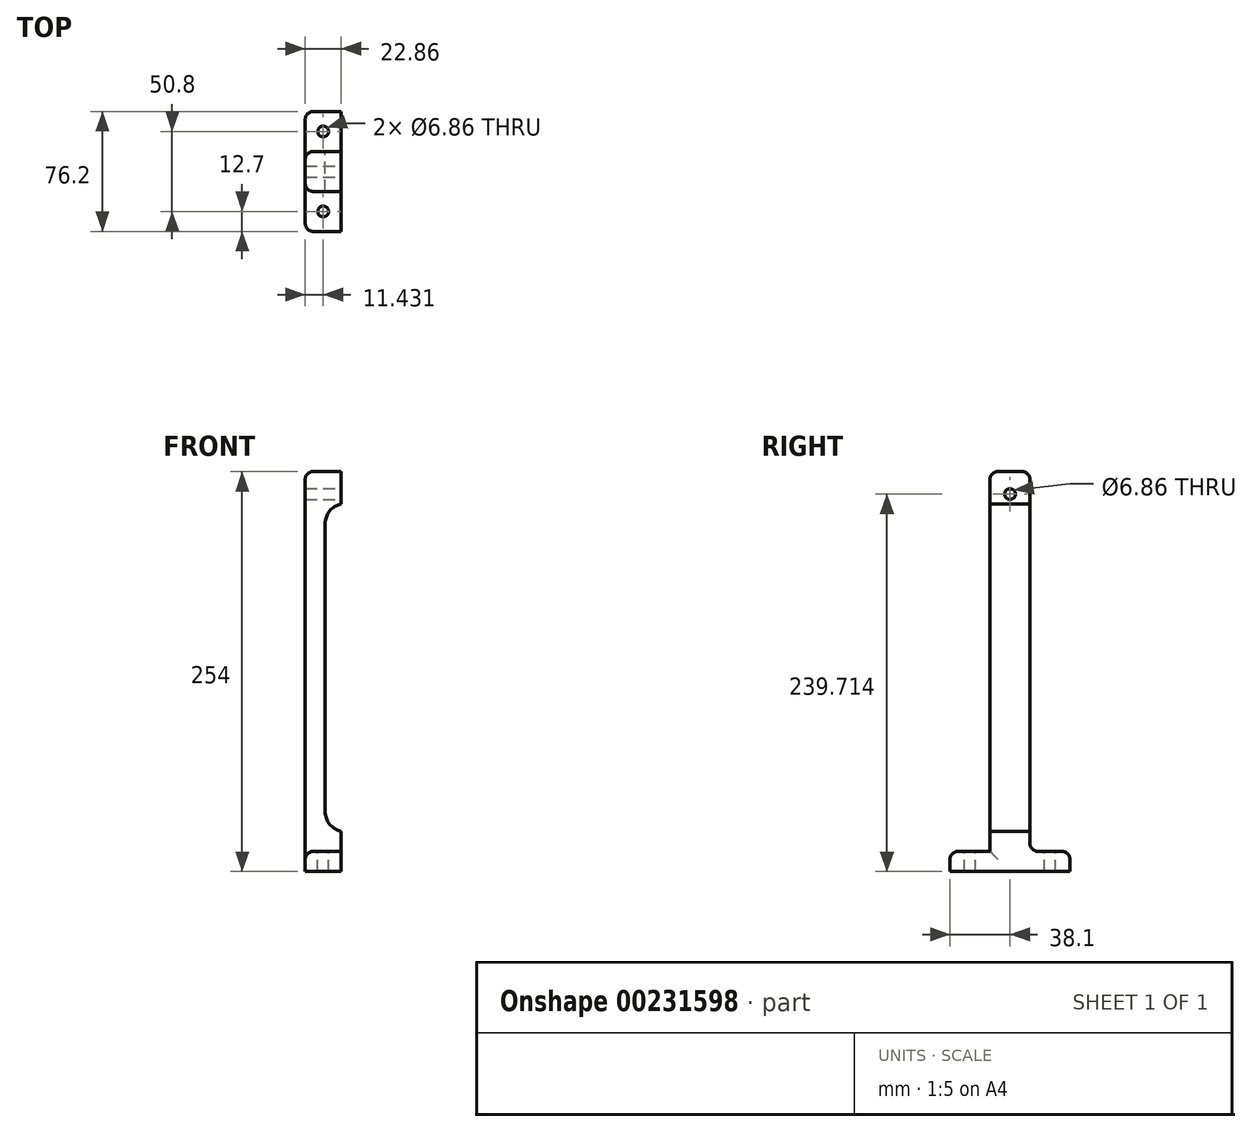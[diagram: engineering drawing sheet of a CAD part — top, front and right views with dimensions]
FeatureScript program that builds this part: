
annotation { "Feature Type Name" : "Feature", "Feature Type Description" : "" }
export const myFeature = defineFeature(function(context is Context, id is Id, definition is map)
    precondition{}
    {
        {
            var Q0;
            Q0=qCreatedBy(makeId("Front.planeOp"),FACE);
            var sketch = newSketch(context, id + "F0", { "sketchPlane" : qUnion([Q0])});
            skLineSegment(sketch, "E0.0", {"start": v(-25.4, 91.14) * mm, "end": v(-25.4, -91.42) * mm});
            skLineSegment(sketch, "E1", {"start": v(-25.4, 91.14) * mm, "end": v(-25.4, 124.52) * mm});
            skLineSegment(sketch, "E2.MirrorCS", {"start": v(-25.4, -91.14) * mm, "end": v(-25.4, -129.48) * mm});
            skArc(sketch, "E3", {"start": v(-2.54, 103.88) * mm, "mid": v(-9.84, 99.47) * mm, "end": v(-12.7, 91.44) * mm});
            skArc(sketch, "E4.MirrorCS", {"start": v(-2.54, -103.88) * mm, "mid": v(-9.84, -99.47) * mm, "end": v(-12.7, -91.44) * mm});
            skLineSegment(sketch, "E5", {"start": v(-12.7, 91.44) * mm, "end": v(-12.7, -91.44) * mm});
            skLineSegment(sketch, "E6.MirrorCS", {"start": v(-2.54, 124.52) * mm, "end": v(-2.54, 103.88) * mm});
            skLineSegment(sketch, "E7", {"start": v(-2.54, -129.48) * mm, "end": v(-25.4, -129.48) * mm});
            skLineSegment(sketch, "E8", {"start": v(-2.54, -103.88) * mm, "end": v(-2.54, -129.48) * mm});
            skLineSegment(sketch, "E9", {"start": v(-25.4, 124.52) * mm, "end": v(-2.54, 124.52) * mm});
            skSolve(sketch);
        }
        {
            var Q0;
            Q0=qSketchRegion(id+"F0",true);
            extrude(context, id + "F1", {"entities" : qUnion([Q0]), "depth" : 25.4 * mm});
        }
        {
            var Q0;
            Q0=makeQuery(id+"F1.opExtrude","SWEPT_FACE",FACE,{"disambiguationData":[OSD([sQuery(id+"F0.wireOp",EDGE,"E6.MirrorCS")])]});
            var sketch = newSketch(context, id + "F2", { "sketchPlane" : qUnion([Q0])});
            skCircle(sketch, "E10", {"center": v(-12.7, 110.23) * mm, "radius": 3.43 * mm});
            skCircle(sketch, "E11.MirrorC", {"center": v(-12.7, -110.23) * mm, "radius": 3.43 * mm});
            skSolve(sketch);
        }
        {
            var Q0;
            Q0=makeQuery(id+"F2.imprint","IMPRINT",FACE,{"disambiguationData":[TD([[makeQuery(id+"F2.imprint","IMPRINT",EDGE,{"derivedFrom":sQuery(id+"F2.wireOp",EDGE,"E11.MirrorC")}),-1.0]])]});
            var Q1;
            Q1=makeQuery(id+"F2.imprint","IMPRINT",FACE,{"disambiguationData":[TD([[makeQuery(id+"F2.imprint","IMPRINT",EDGE,{"derivedFrom":sQuery(id+"F2.wireOp",EDGE,"E10")}),1.0]])]});
            extrude(context, id + "F3", {"entities" : qUnion([Q0, Q1]), "operationType" : NewBodyOperationType.REMOVE, "oppositeDirection" : true, "depth" : 147.32 * mm});
        }
        {
            var Q0;
            Q0=makeQuery(id+"F1.opExtrude","CAP_FACE",FACE,{"disambiguationData":[OSD([sQuery(id+"F0.wireOp",EDGE,"E0.0"),sQuery(id+"F0.wireOp",EDGE,"E1"),sQuery(id+"F0.wireOp",EDGE,"E2.MirrorCS"),sQuery(id+"F0.wireOp",EDGE,"E3"),sQuery(id+"F0.wireOp",EDGE,"E4.MirrorCS"),sQuery(id+"F0.wireOp",EDGE,"E5"),sQuery(id+"F0.wireOp",EDGE,"E6.MirrorCS"),sQuery(id+"F0.wireOp",EDGE,"E7"),sQuery(id+"F0.wireOp",EDGE,"E8"),sQuery(id+"F0.wireOp",EDGE,"E9")])],"isStart":false});
            var sketch = newSketch(context, id + "F4", { "sketchPlane" : qUnion([Q0])});
            skLineSegment(sketch, "E12.bottom", {"start": v(-2.54, -129.48) * mm, "end": v(-25.4, -129.48) * mm});
            skLineSegment(sketch, "E12.top", {"start": v(-2.54, -116.78) * mm, "end": v(-25.4, -116.78) * mm});
            skLineSegment(sketch, "E12.left", {"start": v(-2.54, -129.48) * mm, "end": v(-2.54, -116.78) * mm});
            skLineSegment(sketch, "E12.right", {"start": v(-25.4, -129.48) * mm, "end": v(-25.4, -116.78) * mm});
            skSolve(sketch);
        }
        {
            var Q0;
            Q0=makeQuery(id+"F4.imprint","IMPRINT",FACE,{"disambiguationData":[TD([[makeQuery(id+"F4.imprint","IMPRINT",EDGE,{"derivedFrom":sQuery(id+"F4.wireOp",EDGE,"E12.bottom")}),-1.0]])]});
            extrude(context, id + "F5", {"entities" : qUnion([Q0]), "operationType" : NewBodyOperationType.ADD, "depth" : 25.4 * mm});
        }
        {
            var Q0;
            Q0=makeQuery(id+"F5.opExtrude","CAP_FACE",FACE,{"disambiguationData":[OSD([sQuery(id+"F4.wireOp",EDGE,"E12.bottom"),sQuery(id+"F4.wireOp",EDGE,"E12.top"),sQuery(id+"F4.wireOp",EDGE,"E12.left"),sQuery(id+"F4.wireOp",EDGE,"E12.right")])],"isStart":false});
            extrude(context, id + "F6", {"entities" : qUnion([Q0]), "operationType" : NewBodyOperationType.ADD, "oppositeDirection" : true, "depth" : 76.2 * mm});
        }
        {
            var Q0;
            Q0=makeQuery(id+"F6.opExtrude","SWEPT_FACE",FACE,{"disambiguationData":[OSD([sQuery(id+"F4.wireOp",EDGE,"E12.top")])]});
            var sketch = newSketch(context, id + "F7", { "sketchPlane" : qUnion([Q0])});
            skCircle(sketch, "E13", {"center": v(-13.97, 12.7) * mm, "radius": 3.43 * mm});
            skPoint(sketch, "E13.centerSnap0", {"position": v(-25.4, 12.7) * mm});
            skPoint(sketch, "E13.centerSnap1", {"position": v(-13.97, 25.4) * mm});
            skLineSegment(sketch, "E14", {"start": v(-13.97, 25.4) * mm, "end": v(-13.97, -38.1) * mm});
            skCircle(sketch, "E15", {"center": v(-13.97, -38.1) * mm, "radius": 3.43 * mm});
            skSolve(sketch);
        }
        {
            var Q0;
            {var subQ0=sQuery(id+"F7.wireOp",EDGE,"E14");var subQ1=sQuery(id+"F7.wireOp",EDGE,"E13");var subQ2=makeQuery(id+"F7.imprint","INTERSECT",VERTEX,{"disambiguationData":[OD(0.0)],"derivedFrom":[subQ1,subQ0]});Q0=makeQuery(id+"F7.imprint","IMPRINT",FACE,{"disambiguationData":[TD([[makeQuery(id+"F7.imprint","IMPRINT",EDGE,{"disambiguationData":[TD([[subQ2,-1.0]])],"derivedFrom":subQ1}),1.0]])]});}
            var Q1;
            Q1=makeQuery(id+"F7.imprint","IMPRINT",FACE,{"disambiguationData":[TD([[makeQuery(id+"F7.imprint","IMPRINT",EDGE,{"derivedFrom":sQuery(id+"F7.wireOp",EDGE,"E15")}),1.0]])]});
            var Q2;
            {var subQ0=sQuery(id+"F7.wireOp",EDGE,"E14");var subQ1=sQuery(id+"F7.wireOp",EDGE,"E13");var subQ2=makeQuery(id+"F7.imprint","INTERSECT",VERTEX,{"disambiguationData":[OD(0.0)],"derivedFrom":[subQ1,subQ0]});Q2=makeQuery(id+"F7.imprint","IMPRINT",FACE,{"disambiguationData":[TD([[makeQuery(id+"F7.imprint","IMPRINT",EDGE,{"disambiguationData":[TD([[subQ2,1.0]])],"derivedFrom":subQ1}),1.0]])]});}
            extrude(context, id + "F8", {"entities" : qUnion([Q0, Q1, Q2]), "operationType" : NewBodyOperationType.REMOVE, "oppositeDirection" : true, "depth" : 25.4 * mm});
        }
        {
            var Q0;
            Q0=makeQuery(id+"F1.opExtrude","CAP_EDGE",EDGE,{"disambiguationData":[OSD([sQuery(id+"F0.wireOp",EDGE,"E9")])],"isStart":false});
            var Q1;
            Q1=makeQuery(id+"F1.opExtrude","SWEPT_EDGE",EDGE,{"disambiguationData":[OSD([sQuery(id+"F0.wireOp",EDGE,"E1"),sQuery(id+"F0.wireOp",EDGE,"E9")])]});
            var Q2;
            Q2=makeQuery(id+"F1.opExtrude","CAP_EDGE",EDGE,{"disambiguationData":[OSD([sQuery(id+"F0.wireOp",EDGE,"E9")])],"isStart":true});
            var Q3;
            Q3=makeQuery(id+"F1.opExtrude","CAP_EDGE",EDGE,{"disambiguationData":[OSD([sQuery(id+"F0.wireOp",EDGE,"E0.0"),sQuery(id+"F0.wireOp",EDGE,"E1"),sQuery(id+"F0.wireOp",EDGE,"E2.MirrorCS")])],"isStart":false});
            var Q4;
            Q4=makeQuery(id+"F1.opExtrude","CAP_EDGE",EDGE,{"disambiguationData":[OSD([sQuery(id+"F0.wireOp",EDGE,"E0.0"),sQuery(id+"F0.wireOp",EDGE,"E1"),sQuery(id+"F0.wireOp",EDGE,"E2.MirrorCS")])],"isStart":true});
            var Q5;
            Q5=makeQuery(id+"F6.boolean.opBoolean","INTERSECT",EDGE,{"derivedFrom":[makeQuery(id+"F1.opExtrude","CAP_FACE",FACE,{"disambiguationData":[OSD([sQuery(id+"F0.wireOp",EDGE,"E0.0"),sQuery(id+"F0.wireOp",EDGE,"E1"),sQuery(id+"F0.wireOp",EDGE,"E2.MirrorCS"),sQuery(id+"F0.wireOp",EDGE,"E3"),sQuery(id+"F0.wireOp",EDGE,"E4.MirrorCS"),sQuery(id+"F0.wireOp",EDGE,"E5"),sQuery(id+"F0.wireOp",EDGE,"E6.MirrorCS"),sQuery(id+"F0.wireOp",EDGE,"E7"),sQuery(id+"F0.wireOp",EDGE,"E8"),sQuery(id+"F0.wireOp",EDGE,"E9")])],"isStart":true}),makeQuery(id+"F6.opExtrude","SWEPT_FACE",FACE,{"disambiguationData":[OSD([sQuery(id+"F4.wireOp",EDGE,"E12.top")])]})]});
            var Q6;
            Q6=makeQuery(id+"F6.opExtrude","CAP_EDGE",EDGE,{"disambiguationData":[OSD([sQuery(id+"F4.wireOp",EDGE,"E12.top")])],"isStart":false});
            var Q7;
            Q7=makeQuery(id+"F6.opExtrude","SWEPT_EDGE",EDGE,{"disambiguationData":[OSD([sQuery(id+"F0.wireOp",EDGE,"E0.0"),sQuery(id+"F0.wireOp",EDGE,"E1"),sQuery(id+"F0.wireOp",EDGE,"E2.MirrorCS"),sQuery(id+"F4.wireOp",EDGE,"E12.top"),sQuery(id+"F4.wireOp",EDGE,"E12.right")])]});
            var Q8;
            Q8=makeQuery(id+"F6.opExtrude","CAP_EDGE",EDGE,{"disambiguationData":[OSD([sQuery(id+"F4.wireOp",EDGE,"E12.right")])],"isStart":false});
            var Q9;
            Q9=makeQuery(id+"F5.opExtrude","CAP_EDGE",EDGE,{"disambiguationData":[OSD([sQuery(id+"F4.wireOp",EDGE,"E12.top")])],"isStart":true});
            var Q10;
            Q10=makeQuery(id+"F5.opExtrude","SWEPT_EDGE",EDGE,{"disambiguationData":[OSD([sQuery(id+"F0.wireOp",EDGE,"E0.0"),sQuery(id+"F0.wireOp",EDGE,"E1"),sQuery(id+"F0.wireOp",EDGE,"E2.MirrorCS"),sQuery(id+"F4.wireOp",EDGE,"E12.top"),sQuery(id+"F4.wireOp",EDGE,"E12.right")])]});
            var Q11;
            Q11=makeQuery(id+"F5.opExtrude","CAP_EDGE",EDGE,{"disambiguationData":[OSD([sQuery(id+"F4.wireOp",EDGE,"E12.right")])],"isStart":false});
            var Q12;
            Q12=makeQuery(id+"F5.opExtrude","CAP_EDGE",EDGE,{"disambiguationData":[OSD([sQuery(id+"F4.wireOp",EDGE,"E12.top")])],"isStart":false});
            fillet(context, id + "F9", {"entities" : qUnion([Q0, Q1, Q2, Q3, Q4, Q5, Q6, Q7, Q8, Q9, Q10, Q11, Q12]), "radius" : 5.08 * mm, "tangentPropagation" : true, "allowEdgeOverflow" : false});
        }
    });
